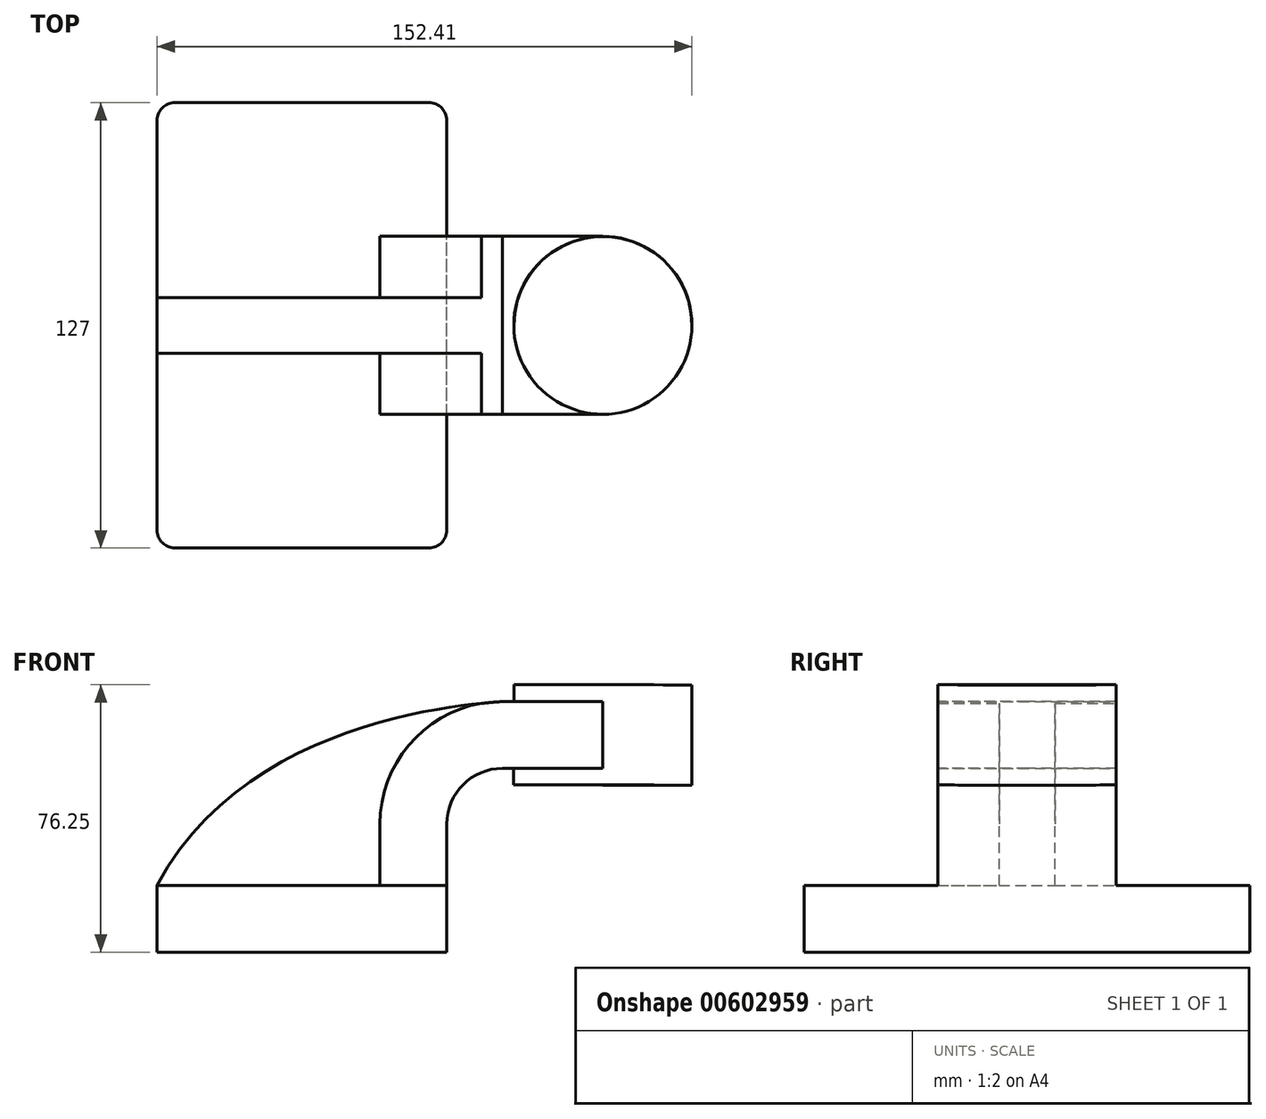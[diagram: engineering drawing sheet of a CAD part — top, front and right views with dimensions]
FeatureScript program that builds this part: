
annotation { "Feature Type Name" : "Feature", "Feature Type Description" : "" }
export const myFeature = defineFeature(function(context is Context, id is Id, definition is map)
    precondition{}
    {
        {
            var Q0;
            Q0=qCreatedBy(makeId("Front.planeOp"),FACE);
            var sketch = newSketch(context, id + "F0", { "sketchPlane" : qUnion([Q0])});
            skLineSegment(sketch, "E0.bottom", {"start": v(41.28, -9.52) * mm, "end": v(-41.28, -9.52) * mm});
            skLineSegment(sketch, "E0.top", {"start": v(41.28, 9.53) * mm, "end": v(-41.28, 9.53) * mm});
            skLineSegment(sketch, "E0.left", {"start": v(41.28, -9.52) * mm, "end": v(41.28, 9.53) * mm});
            skLineSegment(sketch, "E0.right", {"start": v(-41.28, -9.52) * mm, "end": v(-41.28, 9.53) * mm});
            skPoint(sketch, "E0.middle", {"position": v(0, 0) * mm});
            skLineSegment(sketch, "E1.bottom", {"start": v(111.12, 38.1) * mm, "end": v(60.32, 38.1) * mm});
            skLineSegment(sketch, "E1.top", {"start": v(111.12, 66.68) * mm, "end": v(60.32, 66.68) * mm});
            skLineSegment(sketch, "E1.left", {"start": v(111.12, 38.1) * mm, "end": v(111.12, 66.68) * mm});
            skLineSegment(sketch, "E1.right", {"start": v(60.32, 38.1) * mm, "end": v(60.32, 66.68) * mm});
            skPoint(sketch, "E1.middle", {"position": v(85.72, 52.39) * mm});
            skLineSegment(sketch, "E2", {"start": v(41.28, 9.53) * mm, "end": v(41.28, 27) * mm});
            skArc(sketch, "E3", {"start": v(41.27, 27) * mm, "mid": v(45.92, 38.23) * mm, "end": v(57.15, 42.88) * mm});
            skLineSegment(sketch, "E4", {"start": v(57.15, 42.88) * mm, "end": v(85.75, 42.88) * mm});
            skLineSegment(sketch, "E5.0", {"start": v(57.15, 61.93) * mm, "end": v(85.75, 61.93) * mm});
            skArc(sketch, "E5.1", {"start": v(22.23, 27) * mm, "mid": v(32.45, 51.7) * mm, "end": v(57.15, 61.93) * mm});
            skLineSegment(sketch, "E5.2", {"start": v(22.22, 9.53) * mm, "end": v(22.22, 27) * mm});
            skLineSegment(sketch, "E6", {"start": v(85.72, 38.1) * mm, "end": v(85.75, 66.68) * mm});
            skFitSpline(sketch, "E7", {"points": [v(-41.28, 9.52) * mm, v(57.15, 61.93) * mm, v(60.32, 61.93) * mm], "startDerivative": vector(87.92, 165.78) * mm, "endDerivative": vector(15.27, -4.42) * mm});
            skSolve(sketch);
        }
        {
            var Q0;
            Q0=makeQuery(id+"F0.imprint","IMPRINT",FACE,{"disambiguationData":[TD([[makeQuery(id+"F0.imprint","IMPRINT",EDGE,{"derivedFrom":sQuery(id+"F0.wireOp",EDGE,"E0.bottom")}),-1.0]])]});
            extrude(context, id + "F1", {"entities" : qUnion([Q0]), "depth" : 127 * mm, "offsetDistance" : 25.4 * mm, "symmetric" : true});
        }
        {
            var Q0;
            {var subQ1=sQuery(id+"F0.wireOp",EDGE,"E2");Q0=makeQuery(id+"F0.imprint","IMPRINT",FACE,{"disambiguationData":[TD([[makeQuery(id+"F0.imprint","IMPRINT",EDGE,{"derivedFrom":subQ1}),1.0]])]});}
            var Q1;
            {var subQ1=sQuery(id+"F0.wireOp",EDGE,"E1.right");var subQ3=sQuery(id+"F0.wireOp",EDGE,"E4");var subQ4=makeQuery(id+"F0.imprint","INTERSECT",VERTEX,{"derivedFrom":[subQ1,subQ3]});Q1=makeQuery(id+"F0.imprint","IMPRINT",FACE,{"disambiguationData":[TD([[makeQuery(id+"F0.imprint","IMPRINT",EDGE,{"disambiguationData":[TD([[subQ4,-1.0]])],"derivedFrom":subQ3}),1.0]])]});}
            extrude(context, id + "F2", {"entities" : qUnion([Q0, Q1]), "operationType" : NewBodyOperationType.ADD, "depth" : 50.8 * mm, "offsetDistance" : 25.4 * mm, "symmetric" : true});
        }
        {
            var Q0;
            {var subQ3=sQuery(id+"F0.wireOp",EDGE,"E5.2");Q0=makeQuery(id+"F0.imprint","IMPRINT",FACE,{"disambiguationData":[TD([[makeQuery(id+"F0.imprint","IMPRINT",EDGE,{"derivedFrom":subQ3}),1.0]])]});}
            extrude(context, id + "F3", {"entities" : qUnion([Q0]), "operationType" : NewBodyOperationType.ADD, "depth" : 15.88 * mm, "offsetDistance" : 25.4 * mm, "symmetric" : true});
        }
        {
            var Q0;
            {var subQ0=sQuery(id+"F0.wireOp",EDGE,"E1.left");Q0=makeQuery(id+"F0.imprint","IMPRINT",FACE,{"disambiguationData":[TD([[makeQuery(id+"F0.imprint","IMPRINT",EDGE,{"derivedFrom":subQ0}),1.0]])]});}
            var Q1;
            Q1=sQuery(id+"F0.wireOp",EDGE,"E6");
            revolve(context, id + "F4", {"operationType" : NewBodyOperationType.ADD, "entities" : qUnion([Q0]), "axis" : qUnion([Q1]), "revolveType" : RevolveType.FULL});
        }
        {
            var Q0;
            {var subQ1=sQuery(id+"F0.wireOp",EDGE,"E2");Q0=makeQuery(id+"F0.imprint","IMPRINT",FACE,{"disambiguationData":[TD([[makeQuery(id+"F0.imprint","IMPRINT",EDGE,{"derivedFrom":subQ1}),1.0]])]});}
            extrude(context, id + "F5", {"entities" : qUnion([Q0]), "operationType" : NewBodyOperationType.ADD, "depth" : 25.4 * mm, "offsetDistance" : 25.4 * mm, "symmetric" : true});
        }
        {
            var Q0;
            Q0=makeQuery(id+"F1.opExtrude","CAP_EDGE",EDGE,{"disambiguationData":[OSD([sQuery(id+"F0.wireOp",EDGE,"E0.left")])],"isStart":false});
            var Q1;
            Q1=makeQuery(id+"F1.opExtrude","CAP_EDGE",EDGE,{"disambiguationData":[OSD([sQuery(id+"F0.wireOp",EDGE,"E0.right")])],"isStart":false});
            var Q2;
            Q2=makeQuery(id+"F1.opExtrude","CAP_EDGE",EDGE,{"disambiguationData":[OSD([sQuery(id+"F0.wireOp",EDGE,"E0.left")])],"isStart":true});
            var Q3;
            Q3=makeQuery(id+"F1.opExtrude","CAP_EDGE",EDGE,{"disambiguationData":[OSD([sQuery(id+"F0.wireOp",EDGE,"E0.right")])],"isStart":true});
            fillet(context, id + "F6", {"entities" : qUnion([Q0, Q1, Q2, Q3]), "radius" : 5.08 * mm, "tangentPropagation" : true, "allowEdgeOverflow" : false});
        }
    });
